# Revit family: Basin_Catch-Zurn-Z874-IB-InLine
name_source: partatom
category: Plumbing Fixtures
units: mm (PartAtom-declared; Revit-internal decimal feet)

## family parameters
Always vertical = Yes
Cut with Voids When Loaded = No
Maintain Annotation Orientation = No
OmniClass Number = 23.70.50.21.24.14
OmniClass Title = Deck Waste Water Drains
Part Type = Normal
Room Calculation Point = No
Round Connector Dimension = Use Radius
Shared = No
Work Plane-Based = No

## types (24) — shared parameters
Assembly Code = D2040300
CW Connection = No
Default Elevation = 20 "
Description = INLINE CATCH BASIN
Dimension "C" = 32 "
HW Connection = No
Main Material = Polymer - Zurn - HDPE - Grey
Manufacturer = Zurn Water, LLC
Manufacurer Brand = Zurn
Modified Date = 12/18/2025
Product Documentation Link = https://files.zurn.com
Product Installation Sheet URL = https://files.zurn.com
Product Page URL = https://www.zurn.com
Product data url = https://www.bimobject.com
URL = www.zurn.com
Vent Connection = No
WFU = 1
Waste Connection = Yes
zero-valued in all types: CWFU, HWFU

## per-type parameters (varying)
| type | Bottom Outlet | Connector Radius | Dimension "A" | Dimension "B" | End Outlet | Model | Pipe Size_A Inside Diameter | Pipe Size_A Inside Radius | Pipe Size_A Nominal Diameter | Pipe Size_A Nominal Radius | Pipe Size_A Outer Diameter | Pipe Size_A Outer Radius | Type Comments |
| Z874-12-IB-E4 | No | 2 " | 12 " | 17 " | Yes | Z874-12-IB | 4.026 " | 2.013 " | 4 " | 2 " | 4.5 " | 2.25 " | Z874-12-IB With 4 Inch No-Hub End Outlet |
| Z874-12-IB-E6 | No | 3 " | 12 " | 17 " | Yes | Z874-12-IB | 6.065 " | 3.033 " | 6 " | 3 " | 6.625 " | 3.313 " | Z874-12-IB With 6 Inch No-Hub End Outlet |
| Z874-12-IB-E8 | No | 4 " | 12 " | 17 " | Yes | Z874-12-IB | 7.981 " | 3.991 " | 8 " | 4 " | 8.625 " | 4.313 " | Z874-12-IB With 8 Inch No-Hub End Outlet |
| Z874-18-IB-E4 | No | 2 " | 18 " | 23 " | Yes | Z874-18-IB | 4.026 " | 2.013 " | 4 " | 2 " | 4.5 " | 2.25 " | Z874-18-IB With 4 Inch No-Hub End Outlet |
| Z874-18-IB-E6 | No | 3 " | 18 " | 23 " | Yes | Z874-18-IB | 6.065 " | 3.033 " | 6 " | 3 " | 6.625 " | 3.313 " | Z874-18-IB With 6 Inch No-Hub End Outlet |
| Z874-18-IB-E8 | No | 4 " | 18 " | 23 " | Yes | Z874-18-IB | 7.981 " | 3.991 " | 8 " | 4 " | 8.625 " | 4.313 " | Z874-18-IB With 8 Inch No-Hub End Outlet |
| Z874-18-IB-E12 | No | 6 " | 18 " | 23 " | Yes | Z874-18-IB | 12 " | 6 " | 12 " | 6 " | 12.75 " | 6.375 " | Z874-18-IB With 12 Inch No-Hub End Outlet |
| Z874-21-IB-E4 | No | 2 " | 21.25 " | 26.25 " | Yes | Z874-21-IB | 4.026 " | 2.013 " | 4 " | 2 " | 4.5 " | 2.25 " | Z874-21-IB With 4 Inch No-Hub End Outlet |
| Z874-21-IB-E6 | No | 3 " | 21.25 " | 26.25 " | Yes | Z874-21-IB | 6.065 " | 3.033 " | 6 " | 3 " | 6.625 " | 3.313 " | Z874-21-IB With 6 Inch No-Hub End Outlet |
| Z874-21-IB-E8 | No | 4 " | 21.25 " | 26.25 " | Yes | Z874-21-IB | 7.981 " | 3.991 " | 8 " | 4 " | 8.625 " | 4.313 " | Z874-21-IB With 8 Inch No-Hub End Outlet |
| Z874-21-IB-E12 | No | 6 " | 21.25 " | 26.25 " | Yes | Z874-21-IB | 12 " | 6 " | 12 " | 6 " | 12.75 " | 6.375 " | Z874-21-IB With 12 Inch No-Hub End Outlet |
| Z874-21-IB-E18 | No | 9 " | 21.25 " | 26.25 " | Yes | Z874-21-IB | 16.876 " | 8.438 " | 18 " | 9 " | 18 " | 9 " | Z874-21-IB With 18 Inch No-Hub End Outlet |
| Z874-12-IB-U4 | Yes | 2 " | 12 " | 17 " | No | Z874-12-IB | 4.026 " | 2.013 " | 4 " | 2 " | 4.5 " | 2.25 " | Z874-12-IB With 4 Inch No-Hub Bottom Outlet |
| Z874-12-IB-U6 | Yes | 3 " | 12 " | 17 " | No | Z874-12-IB | 6.065 " | 3.033 " | 6 " | 3 " | 6.625 " | 3.313 " | Z874-12-IB With 6 Inch No-Hub Bottom Outlet |
| Z874-12-IB-U8 | Yes | 4 " | 12 " | 17 " | No | Z874-12-IB | 7.981 " | 3.991 " | 8 " | 4 " | 8.625 " | 4.313 " | Z874-12-IB With 8 Inch No-Hub Bottom Outlet |
| Z874-18-IB-U4 | Yes | 2 " | 18 " | 23 " | No | Z874-18-IB | 4.026 " | 2.013 " | 4 " | 2 " | 4.5 " | 2.25 " | Z874-18-IB With 4 Inch No-Hub Bottom Outlet |
| Z874-18-IB-U6 | Yes | 3 " | 18 " | 23 " | No | Z874-18-IB | 6.065 " | 3.033 " | 6 " | 3 " | 6.625 " | 3.313 " | Z874-18-IB With 6 Inch No-Hub Bottom Outlet |
| Z874-18-IB-U8 | Yes | 4 " | 18 " | 23 " | No | Z874-18-IB | 7.981 " | 3.991 " | 8 " | 4 " | 8.625 " | 4.313 " | Z874-18-IB With 8 Inch No-Hub Bottom Outlet |
| Z874-18-IB-U12 | Yes | 6 " | 18 " | 23 " | No | Z874-18-IB | 12 " | 6 " | 12 " | 6 " | 12.75 " | 6.375 " | Z874-18-IB With 12 Inch No-Hub Bottom Outlet |
| Z874-21-IB-U4 | Yes | 2 " | 21.25 " | 26.25 " | No | Z874-21-IB | 4.026 " | 2.013 " | 4 " | 2 " | 4.5 " | 2.25 " | Z874-21-IB With 4 Inch No-Hub Bottom Outlet |
| Z874-21-IB-U6 | Yes | 3 " | 21.25 " | 26.25 " | No | Z874-21-IB | 6.065 " | 3.033 " | 6 " | 3 " | 6.625 " | 3.313 " | Z874-21-IB With 6 Inch No-Hub Bottom Outlet |
| Z874-21-IB-U8 | Yes | 4 " | 21.25 " | 26.25 " | No | Z874-21-IB | 7.981 " | 3.991 " | 8 " | 4 " | 8.625 " | 4.313 " | Z874-21-IB With 8 Inch No-Hub Bottom Outlet |
| Z874-21-IB-U12 | Yes | 6 " | 21.25 " | 26.25 " | No | Z874-21-IB | 12 " | 6 " | 12 " | 6 " | 12.75 " | 6.375 " | Z874-21-IB With 12 Inch No-Hub Bottom Outlet |
| Z874-21-IB-U18 | Yes | 9 " | 21.25 " | 26.25 " | No | Z874-21-IB | 16.876 " | 8.438 " | 18 " | 9 " | 18 " | 9 " | Z874-21-IB With 18 Inch No-Hub Bottom Outlet |

## geometry (parser evidence)
native form markers: Blend x4, Sweep x2
no freeform markers — native parametric forms only
